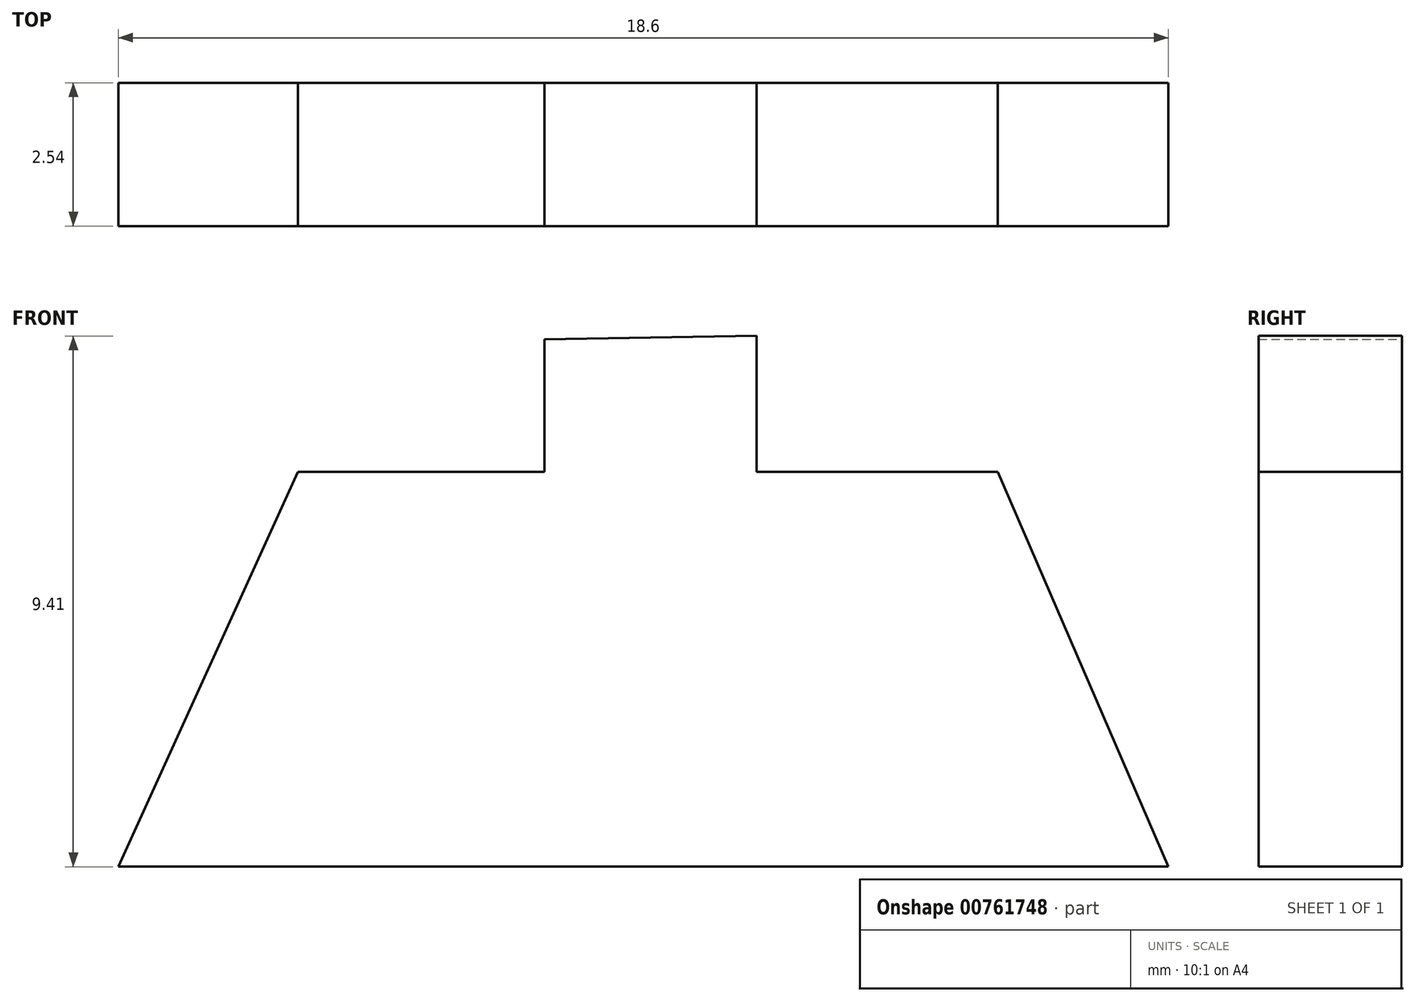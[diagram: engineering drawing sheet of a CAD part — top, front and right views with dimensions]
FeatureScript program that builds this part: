
annotation { "Feature Type Name" : "Feature", "Feature Type Description" : "" }
export const myFeature = defineFeature(function(context is Context, id is Id, definition is map)
    precondition{}
    {
        {
            var Q0;
            Q0=qCreatedBy(makeId("Front.planeOp"),FACE);
            var sketch = newSketch(context, id + "F0", { "sketchPlane" : qUnion([Q0])});
            skLineSegment(sketch, "E0.top", {"start": v(9.3, -27.59) * mm, "end": v(-9.3, -27.59) * mm});
            skPoint(sketch, "E0.middle", {"position": v(0, -22.97) * mm});
            skLineSegment(sketch, "E1", {"start": v(-9.3, -27.59) * mm, "end": v(-6.12, -20.59) * mm});
            skLineSegment(sketch, "E2", {"start": v(-6.12, -20.59) * mm, "end": v(6.28, -20.59) * mm});
            skLineSegment(sketch, "E3", {"start": v(6.28, -20.59) * mm, "end": v(9.3, -27.59) * mm});
            skPoint(sketch, "E4.visualSharp", {"position": v(-9.3, -18.36) * mm});
            skPoint(sketch, "E5.orphan", {"position": v(9.3, -18.36) * mm});
            skLineSegment(sketch, "E6", {"start": v(-1.75, -18.24) * mm, "end": v(-1.75, -20.59) * mm});
            skLineSegment(sketch, "E7", {"start": v(-1.75, -20.59) * mm, "end": v(2, -20.59) * mm});
            skLineSegment(sketch, "E8", {"start": v(2, -20.59) * mm, "end": v(2, -18.18) * mm});
            skPoint(sketch, "E9.center.orphan", {"position": v(0, -10.71) * mm});
            skLineSegment(sketch, "E10", {"start": v(-1.75, -18.24) * mm, "end": v(2, -18.18) * mm});
            skSolve(sketch);
        }
        {
            var Q0;
            Q0=makeQuery(id+"F0.imprint","IMPRINT",FACE,{"disambiguationData":[TD([[makeQuery(id+"F0.imprint","IMPRINT",EDGE,{"derivedFrom":sQuery(id+"F0.wireOp",EDGE,"lVk0FALD-gqSK-UTYr-sGsL-FrxnfIgwRJqC")}),1.0]])]});
            var Q1;
            Q1=makeQuery(id+"F0.imprint","IMPRINT",FACE,{"disambiguationData":[TD([[makeQuery(id+"F0.imprint","IMPRINT",EDGE,{"derivedFrom":sQuery(id+"F0.wireOp",EDGE,"E6")}),1.0]])]});
            var Q2;
            Q2=makeQuery(id+"F0.imprint","IMPRINT",FACE,{"disambiguationData":[TD([[makeQuery(id+"F0.imprint","IMPRINT",EDGE,{"derivedFrom":sQuery(id+"F0.wireOp",EDGE,"E0.top")}),-1.0]])]});
            extrude(context, id + "F1", {"entities" : qUnion([Q0, Q1, Q2]), "depth" : 2.54 * mm, "offsetDistance" : 25.4 * mm});
        }
    });
